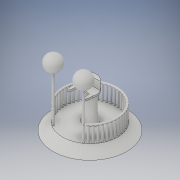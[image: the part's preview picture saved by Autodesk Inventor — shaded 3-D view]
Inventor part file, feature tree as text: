
AUTODESK INVENTOR PART (.ipt)
format: ipt  version: 2017 (Build 210142000, 142)  size: 623,104 bytes
history: native  units: in
note: dims shown in document units (in); Inventor stores cm internally (conversion verified against a paired STEP export)
features: other x20, sketch x10, extrude x6, loft x1, fillet x1
ambient origin geometry x7: Origin, YZ Plane, XY Plane, X Axis, Y Axis, Z Axis, Center Point
bodies: Body1 (feature_tree)
feature tree (38):
  other  "bace + terminal"
  other  "bace of terminal"
  other  "middle workplane"
  other  "middle"
  other  "top workplane"
  loft  "curved tower"
  extrude  "arm rests and terminal monitor"  Depth=0.8in
  other  "middle of the part vertical"
  other  "used to line up the key board and mouse"
  extrude  "bace"  Depth=1.8247in
  other  "ramp around"
  extrude  "railing bars"  Depth=1.0in
  other  "railing bar top workplane"
  other  "railing bar top"
  extrude  "light pole"  Depth=1.2in
  other  "globe light workplane"
  sketch  "Sketch20"  dims[d20=0.85in d27=1.1in]
  other  "light 1"
  other  "light 2"
  extrude  "line up slot"  Depth=1.1in
  other  "mate to back to monitor"
  extrude  "monitor raise"  Depth=1.0in
  sketch  "Sketch26"  dims[d123=1.0in d124=0.0in d134=0.7579in d135=15.748in d137=1.9948in d139=2.0in d140=0.0in d141=0.2749in d142=90.0deg d143=0.25in d144=0.25in d145=90.0deg d146=4.0in d147=0.0in d150=2.0in d151=0.9in d152=2.0in d153=0.9in d155=90.0deg d156=90.0deg d157=0.0in d158=2.0in d159=0.2in d160=0.0in d163=0.8125in d165=0.4167in d166=0.8125in d167=0.4167in d168=0.2083in d169=0.0in d170=1.125in d173=1.8892in d174=1.1844in d175=1.125in d176=1.125in d177=1.1844in d178=1.0in d179=0.0in d180=0.5527in d181=0.01in]
  fillet  "Fillet3"  Radius=0.65in
  other  "bottom workplane"
  other  "top"
  sketch  "Sketch15"  dims[d0=1.0in d1=0.75in]
  sketch  "Sketch16"  dims[d2=1.8247in d3=0.8in]
  sketch  "Sketch17"  dims[d4=0.55in d5=1.8247in]
  other  "Work Axis3"
  other  "Work Axis4"
  sketch  "Sketch18"  dims[d6=0.75in d7=1.0in]
  sketch  "Sketch19"  dims[d8=0.0in d9=90.0deg d10=0.0in d11=90.0deg d12=0.0in d13=90.0deg d19=1.2in]
  other  "Work Axis5"
  other  "Work Axis6"
  sketch  "Sketch21"  dims[d28=0.75in d29=1.0in d30=0.65in]
  sketch  "Sketch23"  dims[d42=1.1in d43=0.85in d44=1.0in d45=0.75in d49=1.2in d50=0.85in d51=1.0in d52=0.75in]
  sketch  "Sketch25"  dims[d122=7.0in]
